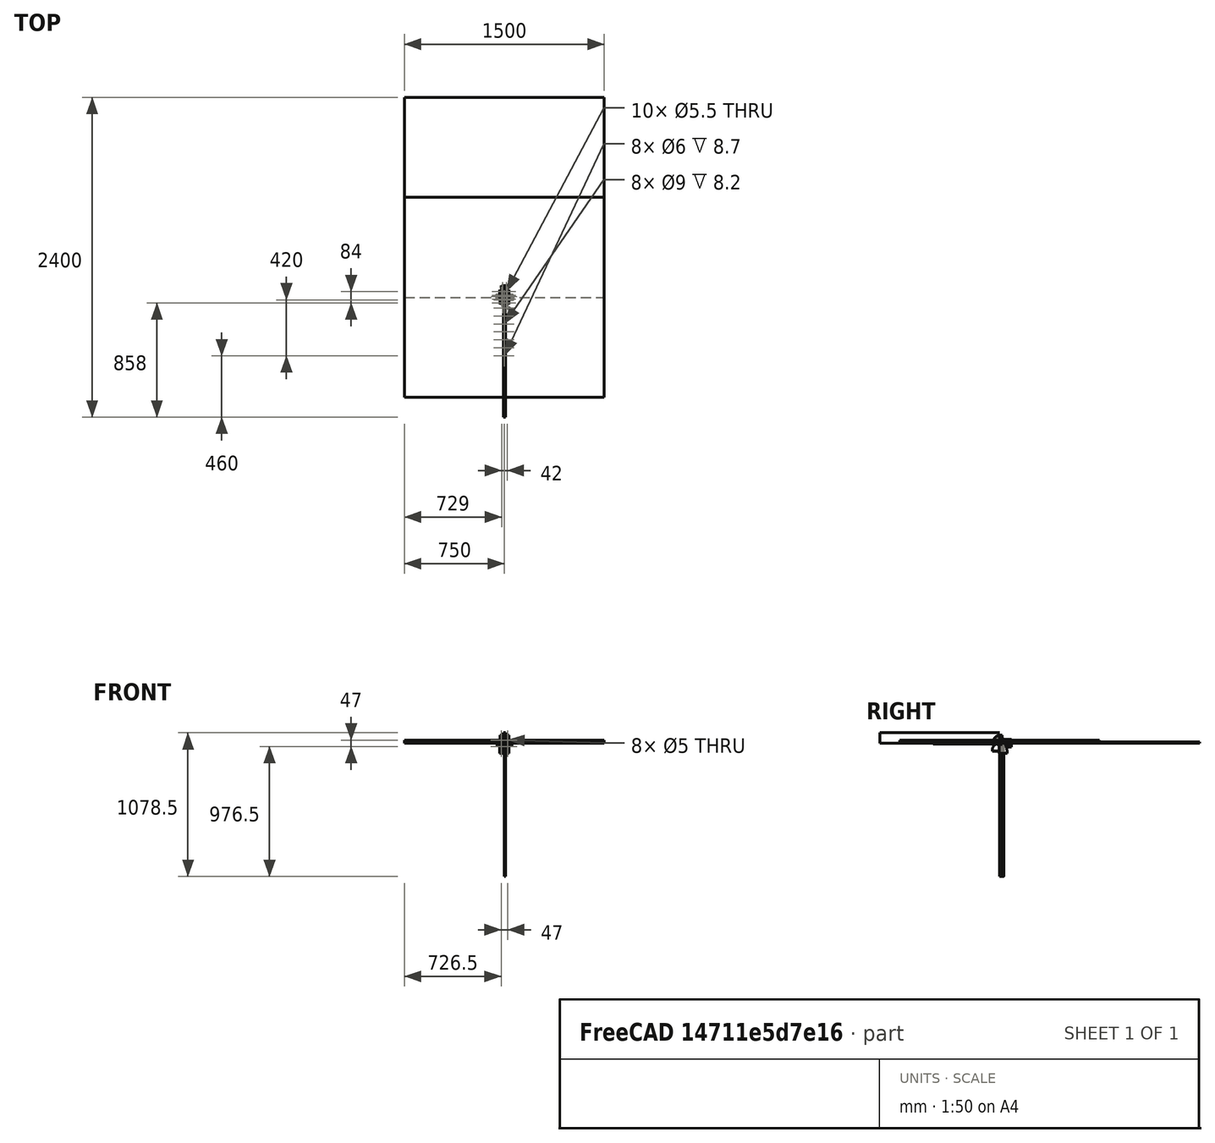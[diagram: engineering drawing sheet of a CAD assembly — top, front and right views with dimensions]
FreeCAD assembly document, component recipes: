
FREECAD ASSEMBLY — COMPONENT RECIPES ("cutting2")

This assembly document has 10 components, labeled P0..P9 below (a component is one placed body or linked part). 7 of them carry a construction recipe — the FreeCAD feature program that regenerates the part from scratch, quoted from this document or its linked companion documents; the rest are supplied as boundary geometry only. No exploded tour is included for this assembly.
COMPONENT P0 — recipe-attached ("p08_bearing_to_plywood", modeled in this document).
Construction recipe (the document's own serialized feature program — sketch geometry with constraints, then the solid features built on it; lengths are millimeters unless a unit is written):

FEATURE [Sketcher::SketchObject] Sketch013
  FullyConstrained = true
  MapMode = 5
  Support = -> [XY_Plane015]
  sketch-geometry (7):
    g0: LineSegment StartX=0 StartY=0 StartZ=0 EndX=27.35 EndY=0 EndZ=0
    g1: LineSegment StartX=27.35 StartY=0 StartZ=0 EndX=27.35 EndY=12.7 EndZ=0
    g2: LineSegment StartX=27.35 StartY=12.7 StartZ=0 EndX=0 EndY=12.7 EndZ=0
    g3: LineSegment StartX=0 StartY=12.7 StartZ=0 EndX=0 EndY=0 EndZ=0
    g4: Circle CenterX=21 CenterY=6.35 CenterZ=0 NormalX=0 NormalY=0 NormalZ=1 AngleXU=0 Radius=2.75
    g5: LineSegment StartX=21 StartY=0 StartZ=0 EndX=21 EndY=6.35 EndZ=0
    g6: LineSegment StartX=21 StartY=6.35 StartZ=0 EndX=21 EndY=12.7 EndZ=0
  constraints (20):
    c: Coincident(g0,g1)
    c: Coincident(g1,g2)
    c: Coincident(g2,g3)
    c: Coincident(g3,g0)
    c: Horizontal(g0)
    c: Horizontal(g2)
    c: Vertical(g1)
    c: Vertical(g3)
    c: Coincident(g0,g-1)
    c: DistanceX(g4) = 21
    c: PointOnObject(g5,g0)
    c: Coincident(g5,g4)
    c: Coincident(g5,g6)
    c: PointOnObject(g6,g2)
    c: Vertical(g6)
    c: Vertical(g5)
    c: Equal(g5,g6)
    c: Diameter(g4) = 5.5
    c: Distance(g3) = 12.7  'length'
    c: DistanceX(g0) = 27.35  'width'
FEATURE [PartDesign::Pad] Pad012
  Direction = (0,0,1)
  Length = 5
  Length2 = 10
  Profile = -> Sketch013
  ReferenceAxis = -> Sketch013 [N_Axis]
  Reversed = true
  Type = 0
FEATURE [Sketcher::SketchObject] Sketch014
  AttachmentOffset = pos=(0,-56,-59.5) rot=(0,0,1;0rad)
  FullyConstrained = true
  MapMode = 5
  Placement = pos=(0,-56,-59.5) rot=(0,0,1;0rad)
  Support = -> [XY_Plane015]
  expr: .AttachmentOffset.Base.y = -.Constraints.length
  expr: .Constraints.length = Sketch010.Constraints[31]
  expr: .Constraints.width = Sketch010.Constraints[30]
  expr: Constraints[33] = Sketch010.Constraints[33]
  sketch-geometry (12):
    g0: LineSegment StartX=0 StartY=0 StartZ=0 EndX=29 EndY=0 EndZ=0
    g1: LineSegment StartX=29 StartY=0 StartZ=0 EndX=29 EndY=56 EndZ=0
    g2: LineSegment StartX=29 StartY=56 StartZ=0 EndX=0 EndY=56 EndZ=0
    g3: LineSegment StartX=0 StartY=56 StartZ=0 EndX=0 EndY=0 EndZ=0
    g4: Circle CenterX=14.5 CenterY=14 CenterZ=0 NormalX=0 NormalY=0 NormalZ=1 AngleXU=0 Radius=2.75
    g5: Circle CenterX=14.5 CenterY=42 CenterZ=0 NormalX=0 NormalY=0 NormalZ=1 AngleXU=0 Radius=2.75
    g6: LineSegment StartX=14.5 StartY=56 StartZ=0 EndX=14.5 EndY=42 EndZ=0
    g7: LineSegment StartX=14.5 StartY=42 StartZ=0 EndX=14.5 EndY=28 EndZ=0
    g8: LineSegment StartX=14.5 StartY=28 StartZ=0 EndX=14.5 EndY=14 EndZ=0
    g9: LineSegment StartX=14.5 StartY=14 StartZ=0 EndX=14.5 EndY=0 EndZ=0
    g10: LineSegment StartX=0 StartY=28 StartZ=0 EndX=14.5 EndY=28 EndZ=0
    g11: LineSegment StartX=14.5 StartY=28 StartZ=0 EndX=29 EndY=28 EndZ=0
  constraints (34):
    c: Coincident(g0,g1)
    c: Coincident(g1,g2)
    c: Coincident(g2,g3)
    c: Coincident(g3,g0)
    c: Horizontal(g0)
    c: Horizontal(g2)
    c: Vertical(g1)
    c: Vertical(g3)
    c: Coincident(g0,g-1)
    c: Vertical(g5,g4)
    c: PointOnObject(g6,g2)
    c: Coincident(g6,g5)
    c: Vertical(g6)
    c: Coincident(g6,g7)
    c: Vertical(g7)
    c: Coincident(g7,g8)
    c: Coincident(g8,g4)
    c: Coincident(g8,g9)
    c: PointOnObject(g9,g0)
    c: Vertical(g9)
    c: Equal(g9,g8)
    c: Equal(g8,g7)
    c: Equal(g7,g6)
    c: PointOnObject(g10,g3)
    c: Coincident(g10,g7)
    c: Horizontal(g10)
    c: Coincident(g10,g11)
    c: PointOnObject(g11,g1)
    c: Horizontal(g11)
    c: Equal(g11,g10)
    c: DistanceX(g0,g0) = 29  'width'
    c: DistanceY(g3,g3) = 56  'length'
    c: Equal(g4,g5)
    c: Diameter(g4) = 5.5
FEATURE [Sketcher::SketchObject] Sketch015
  FullyConstrained = true
  MapMode = 5
  Placement = pos=(0,0,0) rot=(1,0,0;1.5708rad)
  Support = -> [XZ_Plane015]
  expr: Constraints[17] = Sketch013.Constraints[17]
  expr: Constraints[18] = Sketch013.Constraints.length
  expr: Constraints[19] = Sketch013.Constraints.width
  expr: Constraints[23] = Sketch014.AttachmentOffset.Base.z
  expr: Constraints[24] = Sketch014.Constraints.width
  expr: Constraints[9] = Sketch013.Constraints[9]
  sketch-geometry (14):
    g0: LineSegment StartX=0 StartY=0 StartZ=0 EndX=27.35 EndY=0 EndZ=0
    g1: LineSegment StartX=27.35 StartY=0 StartZ=0 EndX=27.35 EndY=12.7 EndZ=0
    g2: LineSegment StartX=27.35 StartY=12.7 StartZ=0 EndX=0 EndY=12.7 EndZ=0
    g3: LineSegment StartX=0 StartY=12.7 StartZ=0 EndX=0 EndY=0 EndZ=0
    g4: Circle CenterX=21 CenterY=6.35 CenterZ=0 NormalX=0 NormalY=0 NormalZ=1 AngleXU=0 Radius=2.75
    g5: LineSegment StartX=21 StartY=0 StartZ=0 EndX=21 EndY=6.35 EndZ=0
    g6: LineSegment StartX=21 StartY=6.35 StartZ=0 EndX=21 EndY=12.7 EndZ=0
    g7: LineSegment StartX=27.35 StartY=0 StartZ=0 EndX=27.35 EndY=-40.764 EndZ=0
    g8: LineSegment StartX=29 StartY=-59.5 StartZ=0 EndX=29 EndY=-54.5 EndZ=0
    g9: ArcOfCircle CenterX=0 CenterY=-54.5 CenterZ=0 NormalX=0 NormalY=0 NormalZ=1 AngleXU=0 Radius=29 StartAngle=0 EndAngle=0.239099
    g10: ArcOfCircle CenterX=56.35 CenterY=-40.764 CenterZ=0 NormalX=0 NormalY=0 NormalZ=1 AngleXU=0 Radius=29 StartAngle=3.14159 EndAngle=3.38069
    g11: LineSegment StartX=27.35 StartY=0 StartZ=0 EndX=0 EndY=0 EndZ=0
    g12: LineSegment StartX=0 StartY=0 StartZ=0 EndX=0 EndY=-59.5 EndZ=0
    g13: LineSegment StartX=0 StartY=-59.5 StartZ=0 EndX=29 EndY=-59.5 EndZ=0
  constraints (39):
    c: Coincident(g0,g1)
    c: Coincident(g1,g2)
    c: Coincident(g2,g3)
    c: Coincident(g3,g0)
    c: Horizontal(g0)
    c: Horizontal(g2)
    c: Vertical(g1)
    c: Vertical(g3)
    c: Coincident(g0,g-1)
    c: DistanceX(g4) = 21
    c: PointOnObject(g5,g0)
    c: Coincident(g5,g4)
    c: Coincident(g5,g6)
    c: PointOnObject(g6,g2)
    c: Vertical(g6)
    c: Vertical(g5)
    c: Equal(g5,g6)
    c: Diameter(g4) = 5.5
    c: Distance(g3) = 12.7
    c: DistanceX(g0) = 27.35
    c: Coincident(g7,g0)
    c: Vertical(g7)
    c: Vertical(g8)
    c: DistanceY(g8) = -59.5
    c: DistanceX(g8) = 29
    c: Distance(g8) = 5
    c: Tangent(g9,g8) = -1.5708
    c: Tangent(g10,g9) = 1.5708
    c: Tangent(g10,g7) = -1.5708
    c: Equal(g9,g10)
    c: PointOnObject(g9,g-2)
    c: Coincident(g7,g11)
    c: PointOnObject(g12,g-2)
    c: PointOnObject(g12,g-2)
    c: Coincident(g12,g13)
    c: Coincident(g13,g8)
    c: Horizontal(g13)
    c: Coincident(g12,g11)
    c: Horizontal(g11)
FEATURE [PartDesign::Pad] Pad013
  BaseFeature = -> Pad012
  Direction = (0,-1,2e-16)
  Length = 5
  Length2 = 10
  Profile = -> Sketch015
  ReferenceAxis = -> Sketch015 [N_Axis]
  Type = 0
FEATURE [PartDesign::Pad] Pad014
  BaseFeature = -> Pad013
  Direction = (0,0,1)
  Length = 5
  Length2 = 10
  Profile = -> Sketch014
  ReferenceAxis = -> Sketch014 [N_Axis]
  Type = 0
FEATURE [Sketcher::SketchObject] Sketch016
  AttachmentOffset = pos=(0,0,24.35) rot=(0,0,1;0rad)
  FullyConstrained = true
  MapMode = 5
  Placement = pos=(24.35,-5.4e-15,5.4e-15) rot=(0.57735,0.57735,0.57735;2.0944rad)
  Support = -> [YZ_Plane015]
  expr: .AttachmentOffset.Base.z = Sketch013.Constraints.width - 3mm
  expr: Constraints[14] = Sketch014.AttachmentOffset.Base.z
  expr: Constraints[15] = Sketch014.Constraints.length
  expr: Constraints[16] = Sketch013.Constraints.length
  sketch-geometry (12):
    g0: LineSegment StartX=-56 StartY=-54.5 StartZ=0 EndX=-56 EndY=-59.5 EndZ=0
    g1: LineSegment StartX=-56 StartY=-59.5 StartZ=0 EndX=0 EndY=-59.5 EndZ=0
    g2: LineSegment StartX=0 StartY=-59.5 StartZ=0 EndX=-2.3e-15 EndY=-17.7 EndZ=0
    g3: LineSegment StartX=12.7 StartY=-5 StartZ=0 EndX=12.7 EndY=0 EndZ=0
    g4: LineSegment StartX=12.7 StartY=0 StartZ=0 EndX=0 EndY=0 EndZ=0
    g5: ArcOfCircle CenterX=0 CenterY=-5 CenterZ=0 NormalX=0 NormalY=0 NormalZ=1 AngleXU=0 Radius=12.7 StartAngle=4.71239 EndAngle=6.28319
    g6: LineSegment StartX=0 StartY=0 StartZ=0 EndX=-5 EndY=0 EndZ=0
    g7: ArcOfEllipse CenterX=-5 CenterY=-54.5 CenterZ=0 NormalX=0 NormalY=0 NormalZ=1 MajorRadius=54.5 MinorRadius=51 AngleXU=1.5708 StartAngle=0 EndAngle=1.5708
    g8: LineSegment StartX=-5 StartY=0 StartZ=0 EndX=-5 EndY=-109 EndZ=0
    g9: LineSegment StartX=-56 StartY=-54.5 StartZ=0 EndX=46 EndY=-54.5 EndZ=0
    g10: GeomPoint X=-5 Y=-35.2841 Z=0
    g11: GeomPoint X=-5 Y=-73.7159 Z=0
  constraints (27):
    c: Vertical(g0)
    c: Coincident(g0,g1)
    c: PointOnObject(g1,g-2)
    c: Horizontal(g1)
    c: Coincident(g1,g2)
    c: PointOnObject(g2,g-2)
    c: PointOnObject(g3,g-1)
    c: Vertical(g3)
    c: Coincident(g3,g4)
    c: Coincident(g4,g-1)
    c: PointOnObject(g5,g-2)
    c: Coincident(g5,g2)
    c: DistanceY(g3,g3) = 5
    c: DistanceY(g0,g0) = 5
    c: DistanceY(g1) = -59.5
    c: Distance(g1) = 56
    c: Distance(g4) = 12.7
    c: Tangent(g5,g3) = -1.5708
    c: Coincident(g6,g4)
    c: PointOnObject(g6,g-1)
    c: Equal(g3,g6)
    c: InternalAlignment(g8-g11 -> g7) x4
    c: Coincident(g7,g9)
    c: Coincident(g7,g0)
    c: Horizontal(g9)
    c: Coincident(g7,g6)
    c: Vertical(g8,g6)
FEATURE [PartDesign::Pad] Pad015
  BaseFeature = -> Pad014
  Direction = (1,-2e-16,3e-16)
  Length = 5
  Length2 = 10
  Profile = -> Sketch016
  ReferenceAxis = -> Sketch016 [N_Axis]
  Type = 0
FEATURE [PartDesign::Mirrored] Mirrored013
  BaseFeature = -> Pad015
  MirrorPlane = -> Sketch013 [V_Axis]
  Originals = -> [Pad012,Pad013,Pad014,Pad015]
FEATURE [PartDesign::Body] Body005  label="p08_bearing_to_plywood"
  Group = -> [Sketch013,Pad012,Sketch014,Sketch015,Pad013,Pad014,Sketch016,Pad015,Mirrored013]
  Origin = -> Origin015
  Tip = -> Mirrored013
COMPONENT P1 — recipe-attached ("bearingTo57BLY", modeled in this document).
Construction recipe (the document's own serialized feature program — sketch geometry with constraints, then the solid features built on it; lengths are millimeters unless a unit is written):

FEATURE [Sketcher::SketchObject] Sketch006
  AttachmentOffset = pos=(0,30,0) rot=(0,0,1;0rad)
  FullyConstrained = true
  MapMode = 5
  Placement = pos=(0,-6.7e-15,30) rot=(1,0,0;1.5708rad)
  Support = -> [XZ_Plane009]
  expr: .AttachmentOffset.Base.y = .Constraints.height
  sketch-geometry (8):
    g0: ArcOfCircle CenterX=0 CenterY=0 CenterZ=0 NormalX=0 NormalY=0 NormalZ=1 AngleXU=0 Radius=19.5 StartAngle=0 EndAngle=1.5708
    g1: LineSegment StartX=28.75 StartY=30 StartZ=0 EndX=28.75 EndY=0 EndZ=0
    g2: LineSegment StartX=19.5 StartY=0 StartZ=0 EndX=28.75 EndY=0 EndZ=0
    g3: LineSegment StartX=23.5 StartY=23.5 StartZ=0 EndX=0 EndY=23.5 EndZ=0
    g4: LineSegment StartX=23.5 StartY=23.5 StartZ=0 EndX=23.5 EndY=0 EndZ=0
    g5: Circle CenterX=23.5 CenterY=23.5 CenterZ=0 NormalX=0 NormalY=0 NormalZ=1 AngleXU=0 Radius=2.75
    g6: LineSegment StartX=28.75 StartY=30 StartZ=0 EndX=0 EndY=30 EndZ=0
    g7: LineSegment StartX=1.2e-15 StartY=19.5 StartZ=0 EndX=0 EndY=30 EndZ=0
  constraints (24):
    c: Coincident(g0,g-1)
    c: PointOnObject(g0,g-1)
    c: PointOnObject(g1,g-1)
    c: Vertical(g1)
    c: Coincident(g2,g0)
    c: Coincident(g2,g1)
    c: PointOnObject(g3,g-2)
    c: Horizontal(g3)
    c: PointOnObject(g4,g-1)
    c: Vertical(g4)
    c: Equal(g4,g3)
    c: DistanceX(g3,g3) = 23.5
    c: Diameter(g0) = 39
    c: DistanceY(g1) = 30  'height'
    c: Coincident(g5,g3)
    c: Coincident(g5,g4)
    c: PointOnObject(g0,g-2)
    c: Coincident(g6,g1)
    c: PointOnObject(g6,g-2)
    c: Horizontal(g6)
    c: Coincident(g7,g0)
    c: Coincident(g7,g6)
    c: Distance(g6) = 28.75  'width'
    c: Diameter(g5) = 5.5
FEATURE [PartDesign::Pad] Pad003
  Direction = (0,-1,-2e-16)
  Length = 5
  Length2 = 10
  Placement = pos=(0,0,0) rot=(1,0,0;1.5708rad)
  Profile = -> Sketch006
  ReferenceAxis = -> Sketch006 [N_Axis]
  Type = 0
FEATURE [PartDesign::Plane] DatumPlane
  AttachmentOffset = pos=(0,0,0) rot=(1,0,0;0.785398rad)
  Length = 86.9918
  MapMode = 5
  Placement = pos=(0,0,0) rot=(1,0,0;0.785398rad)
  ResizeMode = 0
  Support = -> [XY_Plane009]
  Width = 160.206
FEATURE [PartDesign::Mirrored] Mirrored003
  MirrorPlane = -> Sketch006 [V_Axis]
  Placement = pos=(0,0,0) rot=(1,0,0;1.5708rad)
FEATURE [PartDesign::Mirrored] Mirrored004
  MirrorPlane = -> Sketch006 [H_Axis]
  Placement = pos=(0,0,0) rot=(1,0,0;1.5708rad)
FEATURE [PartDesign::MultiTransform] MultiTransform
  BaseFeature = -> Pad003
  Originals = -> [Pad003]
  Placement = pos=(0,0,0) rot=(1,0,0;1.5708rad)
  Transformations = -> [Mirrored003,Mirrored004]
FEATURE [Sketcher::SketchObject] Sketch007
  AttachmentOffset = pos=(0,-29,0) rot=(0,0,1;0rad)
  FullyConstrained = true
  MapMode = 5
  Placement = pos=(0,-29,0) rot=(0,0,1;0rad)
  Support = -> [XY_Plane009]
  expr: .AttachmentOffset.Base.y = -.Constraints.length - 5mm
  expr: .Constraints.width = Sketch006.Constraints.width
  sketch-geometry (7):
    g0: Circle CenterX=18 CenterY=16 CenterZ=0 NormalX=0 NormalY=0 NormalZ=1 AngleXU=0 Radius=2.5
    g1: LineSegment StartX=0 StartY=0 StartZ=0 EndX=28.75 EndY=0 EndZ=0
    g2: LineSegment StartX=28.75 StartY=0 StartZ=0 EndX=28.75 EndY=24 EndZ=0
    g3: LineSegment StartX=28.75 StartY=24 StartZ=0 EndX=0 EndY=24 EndZ=0
    g4: LineSegment StartX=0 StartY=24 StartZ=0 EndX=0 EndY=0 EndZ=0
    g5: LineSegment StartX=18 StartY=16 StartZ=0 EndX=18 EndY=24 EndZ=0
    g6: LineSegment StartX=18 StartY=16 StartZ=0 EndX=28.75 EndY=16 EndZ=0
  constraints (20):
    c: DistanceX(g0) = 18
    c: DistanceY(g0) = 16
    c: Diameter(g0) = 5
    c: Coincident(g1,g2)
    c: Coincident(g2,g3)
    c: Coincident(g3,g4)
    c: Coincident(g4,g1)
    c: Horizontal(g1)
    c: Horizontal(g3)
    c: Vertical(g2)
    c: Vertical(g4)
    c: Coincident(g1,g-1)
    c: Coincident(g5,g0)
    c: PointOnObject(g5,g3)
    c: Vertical(g5)
    c: Coincident(g6,g0)
    c: PointOnObject(g6,g2)
    c: Horizontal(g6)
    c: Distance(g2) = 24  'length'
    c: DistanceX(g2) = 28.75  'width'
FEATURE [PartDesign::AdditiveBox] Box
  AttacherType = Attacher::AttachEngine3D
  AttachmentOffset = pos=(0,-5,-5) rot=(0,0,1;0rad)
  BaseFeature = -> MultiTransform
  Height = 5
  Length = 32.75
  MapMode = 5
  Placement = pos=(0,-5,-5) rot=(0,0,1;0rad)
  Support = -> [XY_Plane008]
  Width = 5
FEATURE [PartDesign::Mirrored] Mirrored005
  BaseFeature = -> Box
  MirrorPlane = -> YZ_Plane009
  Originals = -> [Box]
  Placement = pos=(0,-5,-5) rot=(0,0,1;0rad)
FEATURE [PartDesign::Pad] Pad004
  BaseFeature = -> Mirrored005
  Direction = (0,0,1)
  Length = 5
  Length2 = 10
  Placement = pos=(0,-5,-5) rot=(0,0,1;0rad)
  Profile = -> Sketch007
  ReferenceAxis = -> Sketch007 [N_Axis]
  Reversed = true
  Type = 0
FEATURE [PartDesign::Mirrored] Mirrored006
  MirrorPlane = -> Sketch007 [V_Axis]
  Placement = pos=(0,-5,-5) rot=(0,0,1;0rad)
FEATURE [PartDesign::Mirrored] Mirrored007
  MirrorPlane = -> Sketch007 [H_Axis]
  Placement = pos=(0,-5,-5) rot=(0,0,1;0rad)
FEATURE [PartDesign::MultiTransform] MultiTransform001
  BaseFeature = -> Pad004
  Originals = -> [Pad004]
  Placement = pos=(0,-5,-5) rot=(0,0,1;0rad)
  Transformations = -> [Mirrored006,Mirrored007]
FEATURE [Sketcher::SketchObject] Sketch008
  AttachmentOffset = pos=(0,0,28.75) rot=(0,0,1;0rad)
  FullyConstrained = false
  MapMode = 5
  Placement = pos=(28.75,-6.4e-15,6.4e-15) rot=(0.57735,0.57735,0.57735;2.0944rad)
  Support = -> [YZ_Plane009]
  expr: .AttachmentOffset.Base.z = Sketch006.Constraints.width
  expr: Constraints[12] = -(Sketch007.Constraints.length * 2 + 5mm)
  expr: Constraints[8] = Sketch006.Constraints.height * 2
  sketch-geometry (9):
    g0: LineSegment StartX=0 StartY=60 StartZ=0 EndX=-5 EndY=60 EndZ=0
    g1: LineSegment StartX=-53 StartY=1.12207e-11 StartZ=0 EndX=-53 EndY=-5 EndZ=0
    g2: LineSegment StartX=-53 StartY=-5 StartZ=0 EndX=0 EndY=-5 EndZ=0
    g3: LineSegment StartX=0 StartY=-5 StartZ=0 EndX=0 EndY=60 EndZ=0
    g4: ArcOfEllipse CenterX=9.28498 CenterY=2.81547e-11 CenterZ=0 NormalX=0 NormalY=0 NormalZ=1 MajorRadius=62.285 MinorRadius=61.6431 AngleXU=9.37e-14 StartAngle=1.8022 EndAngle=3.14159
    g5: LineSegment StartX=71.57 StartY=3.43634e-11 StartZ=0 EndX=-53 EndY=1.12207e-11 EndZ=0
    g6: LineSegment StartX=9.28498 StartY=61.6431 StartZ=0 EndX=9.28498 EndY=-61.6431 EndZ=0
    g7: GeomPoint X=18.2036 Y=2.89902e-11 Z=0
    g8: GeomPoint X=0.366367 Y=2.76194e-11 Z=0
  constraints (18):
    c: PointOnObject(g0,g-2)
    c: PointOnObject(g1,g-1)
    c: Coincident(g1,g2)
    c: PointOnObject(g2,g-2)
    c: Horizontal(g2)
    c: Coincident(g2,g3)
    c: Coincident(g3,g0)
    c: DistanceY(g2) = -5
    c: DistanceY(g0) = 60
    c: Vertical(g1)
    c: DistanceX(g0) = -5
    c: Horizontal(g0)
    c: DistanceX(g1) = -53
    c: InternalAlignment(g5-g8 -> g4) x4
    c: Vertical(g6)
    c: Coincident(g4,g1)
    c: Coincident(g4,g0)
    c: Coincident(g5,g1)
FEATURE [PartDesign::Pad] Pad005
  BaseFeature = -> MultiTransform001
  Direction = (1,-2e-16,3e-16)
  Length = 5
  Length2 = 10
  Placement = pos=(0,-5,-5) rot=(0,0,1;0rad)
  Profile = -> Sketch008
  ReferenceAxis = -> Sketch008 [N_Axis]
  Type = 0
FEATURE [PartDesign::Mirrored] Mirrored008
  BaseFeature = -> Pad005
  MirrorPlane = -> YZ_Plane009
  Originals = -> [Pad005]
  Placement = pos=(0,-5,-5) rot=(0,0,1;0rad)
FEATURE [Sketcher::SketchObject] Sketch009
  FullyConstrained = true
  MapMode = 5
  Support = -> [XY_Plane009]
  expr: Constraints[16] = -Sketch007.Constraints.length * 2 - 5mm
  expr: Constraints[17] = Sketch007.Constraints.width
  sketch-geometry (10):
    g0: LineSegment StartX=0 StartY=-72 StartZ=0 EndX=28.75 EndY=-72 EndZ=0
    g1: LineSegment StartX=28.75 StartY=-72 StartZ=0 EndX=28.75 EndY=-53 EndZ=0
    g2: LineSegment StartX=28.75 StartY=-53 StartZ=0 EndX=0 EndY=-53 EndZ=0
    g3: LineSegment StartX=0 StartY=-53 StartZ=0 EndX=0 EndY=-72 EndZ=0
    g4: LineSegment StartX=28.75 StartY=-89 StartZ=0 EndX=0 EndY=-89 EndZ=0
    g5: LineSegment StartX=0 StartY=-89 StartZ=0 EndX=0 EndY=-72 EndZ=0
    g6: Circle CenterX=24.75 CenterY=-80.5 CenterZ=0 NormalX=0 NormalY=0 NormalZ=1 AngleXU=0 Radius=1.375
    g7: Circle CenterX=16.75 CenterY=-80.5 CenterZ=0 NormalX=0 NormalY=0 NormalZ=1 AngleXU=0 Radius=1.375
    g8: LineSegment StartX=28.75 StartY=-72 StartZ=0 EndX=28.75 EndY=-80.5 EndZ=0
    g9: LineSegment StartX=28.75 StartY=-80.5 StartZ=0 EndX=28.75 EndY=-89 EndZ=0
  constraints (29):
    c: Coincident(g0,g1)
    c: Coincident(g1,g2)
    c: Coincident(g2,g3)
    c: Coincident(g3,g0)
    c: Horizontal(g0)
    c: Horizontal(g2)
    c: Vertical(g1)
    c: Vertical(g3)
    c: PointOnObject(g0,g-2)
    c: DistanceY(g0) = -72
    c: Coincident(g1,g8)
    c: Coincident(g9,g4)
    c: PointOnObject(g4,g-2)
    c: Horizontal(g4)
    c: Coincident(g4,g5)
    c: Coincident(g5,g3)
    c: DistanceY(g2) = -53
    c: Distance(g2) = 28.75
    c: Distance(g5) = 17
    c: Coincident(g8,g9)
    c: Vertical(g8)
    c: Vertical(g9)
    c: Equal(g9,g8)
    c: Horizontal(g8,g6)
    c: Horizontal(g6,g7)
    c: Equal(g6,g7)
    c: Diameter(g6) = 2.75
    c: Distance(g6,g8) = 4
    c: Distance(g6,g7) = 8
FEATURE [PartDesign::Pad] Pad006
  BaseFeature = -> Mirrored008
  Direction = (0,0,1)
  Length = 5
  Length2 = 10
  Placement = pos=(0,-5,-5) rot=(0,0,1;0rad)
  Profile = -> Sketch009
  ReferenceAxis = -> Sketch009 [N_Axis]
  Reversed = true
  Type = 0
FEATURE [PartDesign::Body] Body004
  Group = -> [Sketch006,Pad003,DatumPlane,MultiTransform,Mirrored003,Mirrored004,Sketch007,Box,Mirrored005,Pad004,MultiTransform001,Mirrored006,Mirrored007,Sketch008,Pad005,Mirrored008,Sketch009,Pad006]
  Origin = -> Origin009
  Tip = -> Pad006
COMPONENT P2 — geometry summary ("rail"; no construction recipe available for this part):
  bounding box: 500.0 x 20.0 x 17.5 mm
  tessellated surface: 1,522 triangles
  volume: 144383 mm^3 (83% of its bounding box)
  symmetry: 2-fold rotationally symmetric about the y axis; mirror-symmetric across its x mid-plane, z mid-plane
COMPONENT P3 — recipe-attached ("57ToPlywood", modeled in this document).
Construction recipe (the document's own serialized feature program — sketch geometry with constraints, then the solid features built on it; lengths are millimeters unless a unit is written):

FEATURE [PartDesign::CoordinateSystem] LCS_0004
  AttacherType = Attacher::AttachEngine3D
  MapMode = 2
  Support = -> [X_Axis012]
FEATURE [Sketcher::SketchObject] Sketch010
  AttachmentOffset = pos=(0,0,-74.5) rot=(0,0,1;0rad)
  FullyConstrained = true
  MapMode = 5
  Placement = pos=(0,0,-74.5) rot=(0,0,1;0rad)
  Support = -> [XY_Plane012]
  expr: .AttachmentOffset.Base.z = -74.5
  expr: Constraints[30] = Sketch011.Constraints.width
  sketch-geometry (12):
    g0: LineSegment StartX=0 StartY=0 StartZ=0 EndX=29 EndY=0 EndZ=0
    g1: LineSegment StartX=29 StartY=0 StartZ=0 EndX=29 EndY=56 EndZ=0
    g2: LineSegment StartX=29 StartY=56 StartZ=0 EndX=0 EndY=56 EndZ=0
    g3: LineSegment StartX=0 StartY=56 StartZ=0 EndX=0 EndY=0 EndZ=0
    g4: Circle CenterX=14.5 CenterY=14 CenterZ=0 NormalX=0 NormalY=0 NormalZ=1 AngleXU=0 Radius=2.75
    g5: Circle CenterX=14.5 CenterY=42 CenterZ=0 NormalX=0 NormalY=0 NormalZ=1 AngleXU=0 Radius=2.75
    g6: LineSegment StartX=14.5 StartY=56 StartZ=0 EndX=14.5 EndY=42 EndZ=0
    g7: LineSegment StartX=14.5 StartY=42 StartZ=0 EndX=14.5 EndY=28 EndZ=0
    g8: LineSegment StartX=14.5 StartY=28 StartZ=0 EndX=14.5 EndY=14 EndZ=0
    g9: LineSegment StartX=14.5 StartY=14 StartZ=0 EndX=14.5 EndY=0 EndZ=0
    g10: LineSegment StartX=0 StartY=28 StartZ=0 EndX=14.5 EndY=28 EndZ=0
    g11: LineSegment StartX=14.5 StartY=28 StartZ=0 EndX=29 EndY=28 EndZ=0
  constraints (34):
    c: Coincident(g0,g1)
    c: Coincident(g1,g2)
    c: Coincident(g2,g3)
    c: Coincident(g3,g0)
    c: Horizontal(g0)
    c: Horizontal(g2)
    c: Vertical(g1)
    c: Vertical(g3)
    c: Coincident(g0,g-1)
    c: Vertical(g5,g4)
    c: PointOnObject(g6,g2)
    c: Coincident(g6,g5)
    c: Vertical(g6)
    c: Coincident(g6,g7)
    c: Vertical(g7)
    c: Coincident(g7,g8)
    c: Coincident(g8,g4)
    c: Coincident(g8,g9)
    c: PointOnObject(g9,g0)
    c: Vertical(g9)
    c: Equal(g9,g8)
    c: Equal(g8,g7)
    c: Equal(g7,g6)
    c: PointOnObject(g10,g3)
    c: Coincident(g10,g7)
    c: Horizontal(g10)
    c: Coincident(g10,g11)
    c: PointOnObject(g11,g1)
    c: Horizontal(g11)
    c: Equal(g11,g10)
    c: DistanceX(g0,g0) = 29
    c: DistanceY(g3,g3) = 56
    c: Equal(g4,g5)
    c: Diameter(g4) = 5.5
FEATURE [Sketcher::SketchObject] Sketch011
  FullyConstrained = true
  MapMode = 5
  Placement = pos=(0,0,0) rot=(1,0,0;1.5708rad)
  Support = -> [XZ_Plane012]
  sketch-geometry (8):
    g0: Circle CenterX=23.5 CenterY=23.5 CenterZ=0 NormalX=0 NormalY=0 NormalZ=1 AngleXU=0 Radius=2.5
    g1: LineSegment StartX=29 StartY=29 StartZ=0 EndX=0 EndY=29 EndZ=0
    g2: LineSegment StartX=29 StartY=29 StartZ=0 EndX=29 EndY=0 EndZ=0
    g3: ArcOfCircle CenterX=0 CenterY=0 CenterZ=0 NormalX=0 NormalY=0 NormalZ=1 AngleXU=0 Radius=20 StartAngle=0 EndAngle=1.5708
    g4: LineSegment StartX=20 StartY=0 StartZ=0 EndX=29 EndY=0 EndZ=0
    g5: LineSegment StartX=1.2e-15 StartY=20 StartZ=0 EndX=0 EndY=29 EndZ=0
    g6: LineSegment StartX=0 StartY=0 StartZ=0 EndX=29 EndY=0 EndZ=0
    g7: LineSegment StartX=0 StartY=0 StartZ=0 EndX=0 EndY=29 EndZ=0
  constraints (22):
    c: PointOnObject(g1,g-2)
    c: Horizontal(g1)
    c: Coincident(g3,g-1)
    c: PointOnObject(g3,g-2)
    c: PointOnObject(g3,g-1)
    c: Diameter(g3) = 40
    c: Coincident(g4,g3)
    c: Coincident(g4,g2)
    c: Horizontal(g4)
    c: Coincident(g5,g3)
    c: Coincident(g5,g1)
    c: DistanceX(g0) = 23.5
    c: DistanceY(g0) = 23.5
    c: Diameter(g0) = 5
    c: Vertical(g2)
    c: Coincident(g6,g3)
    c: Coincident(g6,g2)
    c: Coincident(g7,g3)
    c: Coincident(g7,g1)
    c: Equal(g6,g7)
    c: Distance(g6) = 29  'width'
    c: Coincident(g2,g1)
FEATURE [PartDesign::Pad] Pad007
  Direction = (0,-1,-2e-16)
  Length = 5
  Length2 = 10
  Placement = pos=(0,0,0) rot=(1,0,0;1.5708rad)
  Profile = -> Sketch011
  ReferenceAxis = -> Sketch011 [N_Axis]
  Type = 0
FEATURE [PartDesign::Mirrored] Mirrored009
  MirrorPlane = -> Sketch011 [V_Axis]
  Placement = pos=(0,0,0) rot=(1,0,0;1.5708rad)
FEATURE [PartDesign::Mirrored] Mirrored010
  MirrorPlane = -> Sketch011 [H_Axis]
  Placement = pos=(0,0,0) rot=(1,0,0;1.5708rad)
FEATURE [PartDesign::MultiTransform] MultiTransform002
  BaseFeature = -> Pad007
  Originals = -> [Pad007]
  Placement = pos=(0,0,0) rot=(1,0,0;1.5708rad)
  Transformations = -> [Mirrored009,Mirrored010]
FEATURE [Sketcher::SketchObject] Sketch_1
  FullyConstrained = true
  MapMode = 5
  Placement = pos=(0,0,0) rot=(1,0,0;1.5708rad)
  Support = -> [XZ_Plane012]
  expr: Constraints[10] = Sketch010.AttachmentOffset.Base.z
  expr: Constraints[11] = -Sketch011.Constraints.width
  expr: Constraints[9] = Sketch011.Constraints.width
  sketch-geometry (4):
    g0: LineSegment StartX=0 StartY=-29 StartZ=0 EndX=29 EndY=-29 EndZ=0
    g1: LineSegment StartX=29 StartY=-29 StartZ=0 EndX=29 EndY=-74.5 EndZ=0
    g2: LineSegment StartX=29 StartY=-74.5 StartZ=0 EndX=0 EndY=-74.5 EndZ=0
    g3: LineSegment StartX=0 StartY=-74.5 StartZ=0 EndX=0 EndY=-29 EndZ=0
  constraints (12):
    c: Coincident(g0,g1)
    c: Coincident(g1,g2)
    c: Coincident(g2,g3)
    c: Coincident(g3,g0)
    c: Horizontal(g0)
    c: Horizontal(g2)
    c: Vertical(g1)
    c: Vertical(g3)
    c: PointOnObject(g0,g-2)
    c: Distance(g0) = 29
    c: DistanceY(g2) = -74.5
    c: DistanceY(g0) = -29
FEATURE [PartDesign::Pad] Pad008
  BaseFeature = -> MultiTransform002
  Direction = (0,-1,-2e-16)
  Length = 5
  Length2 = 10
  Placement = pos=(0,0,0) rot=(1,0,0;1.5708rad)
  Profile = -> Sketch_1
  ReferenceAxis = -> Sketch_1 [N_Axis]
  Type = 0
FEATURE [PartDesign::Pad] Pad009
  BaseFeature = -> Pad008
  Direction = (0,0,1)
  Length = 5
  Length2 = 10
  Placement = pos=(0,0,0) rot=(1,0,0;1.5708rad)
  Profile = -> Sketch010
  ReferenceAxis = -> Sketch010 [N_Axis]
  Type = 0
FEATURE [PartDesign::Mirrored] Mirrored011
  BaseFeature = -> Pad009
  MirrorPlane = -> Sketch_1 [V_Axis]
  Originals = -> [Pad008,Pad009]
  Placement = pos=(0,0,0) rot=(1,0,0;1.5708rad)
FEATURE [Sketcher::SketchObject] Sketch012
  AttachmentOffset = pos=(0,0,29) rot=(0,0,1;0rad)
  FullyConstrained = true
  MapMode = 5
  Placement = pos=(29,-6.4e-15,6.4e-15) rot=(0.57735,0.57735,0.57735;2.0944rad)
  Support = -> [YZ_Plane012]
  expr: .AttachmentOffset.Base.z = Sketch011.Constraints.width
  expr: Constraints[10] = Sketch010.AttachmentOffset.Base.z + 5mm
  expr: Constraints[12] = 56
  expr: Constraints[9] = Sketch011.Constraints.width
  sketch-geometry (9):
    g0: LineSegment StartX=0 StartY=29 StartZ=0 EndX=-5 EndY=29 EndZ=0
    g1: LineSegment StartX=-5 StartY=29 StartZ=0 EndX=-5 EndY=-74.5 EndZ=0
    g2: LineSegment StartX=-5 StartY=-74.5 StartZ=0 EndX=56 EndY=-74.5 EndZ=0
    g3: LineSegment StartX=56 StartY=-74.5 StartZ=0 EndX=56 EndY=-69.5 EndZ=0
    g4: ArcOfEllipse CenterX=0 CenterY=-69.5 CenterZ=0 NormalX=0 NormalY=0 NormalZ=1 MajorRadius=98.5 MinorRadius=56 AngleXU=-1.5708 StartAngle=1.5708 EndAngle=3.14159
    g5: LineSegment StartX=0 StartY=-168 StartZ=0 EndX=0 EndY=29 EndZ=0
    g6: LineSegment StartX=56 StartY=-69.5 StartZ=0 EndX=-56 EndY=-69.5 EndZ=0
    g7: GeomPoint X=0 Y=-150.532 Z=0
    g8: GeomPoint X=0 Y=11.5324 Z=0
  constraints (19):
    c: PointOnObject(g0,g-2)
    c: Coincident(g0,g1)
    c: Vertical(g1)
    c: Coincident(g1,g2)
    c: Horizontal(g2)
    c: Coincident(g2,g3)
    c: Vertical(g3)
    c: Horizontal(g0)
    c: Equal(g3,g0)
    c: DistanceY(g0) = 29
    c: DistanceY(g3) = -69.5
    c: Distance(g3) = 5
    c: DistanceX(g3) = 56
    c: InternalAlignment(g5-g8 -> g4) x4
    c: PointOnObject(g4,g-2)
    c: Coincident(g4,g0)
    c: Coincident(g4,g3)
    c: Vertical(g5)
    c: DistanceY(g1,g4) = 5
FEATURE [PartDesign::Pad] Pad010
  BaseFeature = -> Mirrored011
  Direction = (1,-2e-16,3e-16)
  Length = 5
  Length2 = 10
  Placement = pos=(0,0,0) rot=(1,0,0;1.5708rad)
  Profile = -> Sketch012
  ReferenceAxis = -> Sketch012 [N_Axis]
  Type = 0
FEATURE [PartDesign::Mirrored] Mirrored012
  BaseFeature = -> Pad010
  MirrorPlane = -> YZ_Plane012
  Originals = -> [Pad010]
  Placement = pos=(0,0,0) rot=(1,0,0;1.5708rad)
FEATURE [PartDesign::CoordinateSystem] Local_CS  label="fixture_plane"
  AttacherType = Attacher::AttachEngine3D
  AttachmentOffset = pos=(0,0,0) rot=(-1,0,0;1.5708rad)
  MapMode = 5
  Placement = pos=(0,0,0) rot=(-1,0,0;1.5708rad)
  Support = -> [XY_Plane012]
FEATURE [PartDesign::Body] _7ToPlywood  label="57ToPlywood"
  Group = -> [LCS_0004,Sketch010,Sketch011,Pad007,MultiTransform002,Mirrored009,Mirrored010,Sketch_1,Pad008,Pad009,Mirrored011,Sketch012,Pad010,Mirrored012,Local_CS]
  Origin = -> Origin012
  Tip = -> Mirrored012
COMPONENT P4 — recipe-attached ("bearing", modeled in this document).
Construction recipe (the document's own serialized feature program — sketch geometry with constraints, then the solid features built on it; lengths are millimeters unless a unit is written):

FEATURE [Sketcher::SketchObject] Sketch
  FullyConstrained = false
  MapMode = 5
  Placement = pos=(0,0,0) rot=(1,0,0;1.5708rad)
  Support = -> [XZ_Plane]
  sketch-geometry (12):
    g0: LineSegment StartX=0 StartY=23 StartZ=0 EndX=0 EndY=0 EndZ=0
    g1: ArcOfCircle CenterX=0 CenterY=33 CenterZ=0 NormalX=0 NormalY=0 NormalZ=1 AngleXU=0 Radius=10 StartAngle=4.71239 EndAngle=7.85398
    g2: ArcOfCircle CenterX=0 CenterY=33 CenterZ=0 NormalX=0 NormalY=0 NormalZ=1 AngleXU=0 Radius=29 StartAngle=0.169407 EndAngle=1.5708
    g3: ArcOfCircle CenterX=62.5 CenterY=12.5 CenterZ=0 NormalX=0 NormalY=0 NormalZ=1 AngleXU=0 Radius=2.5 StartAngle=0 EndAngle=1.5708
    g4: LineSegment StartX=0 StartY=0 StartZ=0 EndX=65 EndY=0 EndZ=0
    g5: LineSegment StartX=65 StartY=0 StartZ=0 EndX=65 EndY=12.5 EndZ=0
    g6: LineSegment StartX=3.1e-15 StartY=43 StartZ=0 EndX=0 EndY=62 EndZ=0
    g7: LineSegment StartX=17 StartY=33 StartZ=0 EndX=17 EndY=0 EndZ=0
    g8: LineSegment StartX=32.5 StartY=15 StartZ=0 EndX=47.5 EndY=15 EndZ=0
    g9: LineSegment StartX=47.5 StartY=15 StartZ=0 EndX=62.5 EndY=15 EndZ=0
    g10: LineSegment StartX=47.5 StartY=0 StartZ=0 EndX=47.5 EndY=15 EndZ=0
    g11: LineSegment StartX=32.5 StartY=15 StartZ=0 EndX=28.5849 EndY=37.8893 EndZ=0
  constraints (33):
    c: PointOnObject(g0,g-2)
    c: Coincident(g0,g-1)
    c: PointOnObject(g1,g-2)
    c: Coincident(g1,g0)
    c: PointOnObject(g1,g-2)
    c: Coincident(g2,g1)
    c: PointOnObject(g2,g-2)
    c: Coincident(g4,g0)
    c: PointOnObject(g4,g-1)
    c: Coincident(g5,g4)
    c: Vertical(g5)
    c: Coincident(g6,g1)
    c: Coincident(g6,g2)
    c: Tangent(g5,g3) = -1.5708
    c: Tangent(g9,g3) = 1.5708
    c: PointOnObject(g7,g-1)
    c: Vertical(g7)
    c: Diameter(g1) = 20  'd'
    c: Coincident(g8,g9)
    c: Horizontal(g8)
    c: Horizontal(g9)
    c: Equal(g8,g9)
    c: PointOnObject(g10,g-1)
    c: Coincident(g10,g8)
    c: Vertical(g10)
    c: Distance(g10) = 15  'fixture_hole_height'
    c: DistanceX(g10) = 47.5  'hole_d_x2'
    c: DistanceX(g4) = 65  'width_x2'
    c: DistanceY(g1) = 33
    c: DistanceY(g2) = 62
    c: Coincident(g11,g8)
    c: Tangent(g11,g2) = -1.5708
    c: Diameter(g3) = 5
FEATURE [PartDesign::Pad] Pad  label="bearing_fixture_pad"
  Direction = (0,-1,-2e-16)
  Length = 40
  Length2 = 10
  Midplane = true
  Placement = pos=(0,0,0) rot=(1,0,0;1.5708rad)
  Profile = -> Sketch
  ReferenceAxis = -> Sketch [N_Axis]
  Type = 0
FEATURE [Sketcher::SketchObject] Sketch001
  FullyConstrained = true
  MapMode = 5
  Support = -> [XY_Plane]
  expr: Constraints[14] = Sketch.Constraints.hole_d_x2
  sketch-geometry (7):
    g0: ArcOfCircle CenterX=45 CenterY=0 CenterZ=0 NormalX=0 NormalY=0 NormalZ=1 AngleXU=0 Radius=5 StartAngle=1.5708 EndAngle=4.71239
    g1: ArcOfCircle CenterX=50 CenterY=0 CenterZ=0 NormalX=0 NormalY=0 NormalZ=1 AngleXU=0 Radius=5 StartAngle=4.71239 EndAngle=7.85398
    g2: LineSegment StartX=45 StartY=-5 StartZ=0 EndX=50 EndY=-5 EndZ=0
    g3: LineSegment StartX=50 StartY=5 StartZ=0 EndX=45 EndY=5 EndZ=0
    g4: GeomPoint X=40 Y=0 Z=0
    g5: GeomPoint X=55 Y=0 Z=0
    g6: GeomPoint X=47.5 Y=0 Z=0
  constraints (15):
    c: Tangent(g0,g2) = -1.5708
    c: Tangent(g2,g1) = -1.5708
    c: Tangent(g1,g3) = -1.5708
    c: Tangent(g3,g0) = -1.5708
    c: Equal(g0,g1)
    c: PointOnObject(g0,g-1)
    c: PointOnObject(g1,g-1)
    c: PointOnObject(g4,g0)
    c: PointOnObject(g5,g1)
    c: PointOnObject(g5,g-1)
    c: PointOnObject(g4,g-1)
    c: Diameter(g1) = 10
    c: DistanceX(g4,g5) = 15
    c: Symmetric(g0,g1,g6)
    c: DistanceX(g6) = 47.5
FEATURE [PartDesign::Pocket] Pocket
  BaseFeature = -> Pad
  Direction = (0,0,-1)
  Length = 5
  Length2 = 5
  Placement = pos=(0,0,0) rot=(1,0,0;1.5708rad)
  Profile = -> Sketch001
  ReferenceAxis = -> Sketch001 [N_Axis]
  Reversed = true
  Type = 1
FEATURE [PartDesign::Mirrored] Mirrored
  BaseFeature = -> Pocket
  MirrorPlane = -> Sketch [V_Axis]
  Originals = -> [Pad,Pocket]
  Placement = pos=(0,0,0) rot=(1,0,0;1.5708rad)
FEATURE [PartDesign::Fillet] Fillet
  Base = -> Mirrored [Edge18,Edge9]
  BaseFeature = -> Mirrored
  Placement = pos=(0,0,0) rot=(1,0,0;1.5708rad)
  Radius = 4
  SupportTransform = false
  UseAllEdges = false
FEATURE [PartDesign::Body] Body  label="bearing_fixture_body"
  Group = -> [Sketch,Pad,Sketch001,Pocket,Mirrored,Fillet]
  Origin = -> Origin
  Tip = -> Fillet
FEATURE [Sketcher::SketchObject] Sketch003
  FullyConstrained = true
  MapMode = 5
  Support = -> [XY_Plane001]
  expr: Constraints[11] = Sketch001.Constraints[11]
  expr: Constraints[12] = Sketch001.Constraints[12]
  expr: Constraints[14] = Sketch001.Constraints[14]
  expr: Constraints[26] = Sketch.Constraints.width_x2
  expr: Constraints[27] = Pad.Length
  sketch-geometry (12):
    g0: ArcOfCircle CenterX=45 CenterY=0 CenterZ=0 NormalX=0 NormalY=0 NormalZ=1 AngleXU=0 Radius=5 StartAngle=1.5708 EndAngle=4.71239
    g1: ArcOfCircle CenterX=50 CenterY=0 CenterZ=0 NormalX=0 NormalY=0 NormalZ=1 AngleXU=0 Radius=5 StartAngle=4.71239 EndAngle=7.85398
    g2: LineSegment StartX=45 StartY=-5 StartZ=0 EndX=50 EndY=-5 EndZ=0
    g3: LineSegment StartX=50 StartY=5 StartZ=0 EndX=45 EndY=5 EndZ=0
    g4: GeomPoint X=40 Y=0 Z=0
    g5: GeomPoint X=55 Y=0 Z=0
    g6: GeomPoint X=47.5 Y=0 Z=0
    g7: LineSegment StartX=65 StartY=-20 StartZ=0 EndX=65 EndY=20 EndZ=0
    g8: LineSegment StartX=65 StartY=20 StartZ=0 EndX=0 EndY=20 EndZ=0
    g9: LineSegment StartX=0 StartY=20 StartZ=0 EndX=0 EndY=-20 EndZ=0
    g10: LineSegment StartX=0 StartY=-20 StartZ=0 EndX=65 EndY=-20 EndZ=0
    g11: GeomPoint X=32.5 Y=0 Z=0
  constraints (28):
    c: Tangent(g0,g2) = -1.5708
    c: Tangent(g2,g1) = -1.5708
    c: Tangent(g1,g3) = -1.5708
    c: Tangent(g3,g0) = -1.5708
    c: Equal(g0,g1)
    c: PointOnObject(g0,g-1)
    c: PointOnObject(g1,g-1)
    c: PointOnObject(g4,g0)
    c: PointOnObject(g5,g1)
    c: PointOnObject(g5,g-1)
    c: PointOnObject(g4,g-1)
    c: Diameter(g1) = 10
    c: DistanceX(g4,g5) = 15
    c: Symmetric(g0,g1,g6)
    c: DistanceX(g6) = 47.5
    c: Coincident(g7,g8)
    c: Coincident(g8,g9)
    c: Coincident(g9,g10)
    c: Coincident(g10,g7)
    c: Horizontal(g8)
    c: Horizontal(g10)
    c: Vertical(g7)
    c: Vertical(g9)
    c: Symmetric(g8,g7,g11)
    c: PointOnObject(g11,g-1)
    c: PointOnObject(g8,g-2)
    c: Distance(g-1,g7) = 65
    c: DistanceY(g9,g9) = 40
FEATURE [PartDesign::Pad] Pad001  label="insertion_pad"
  Direction = (0,0,1)
  Length = 8
  Length2 = 10
  Profile = -> Sketch003
  ReferenceAxis = -> Sketch003 [N_Axis]
  Reversed = true
  Type = 0
FEATURE [PartDesign::Mirrored] Mirrored001
  BaseFeature = -> Pad001
  MirrorPlane = -> Sketch003 [V_Axis]
  Originals = -> [Pad001]
FEATURE [PartDesign::Body] Body001  label="insertion_body"
  Group = -> [Sketch003,Pad001,Mirrored001]
  Origin = -> Origin001
  Tip = -> Mirrored001
COMPONENT P5 — geometry summary ("linear_bearing"; no construction recipe available for this part):
  bounding box: 78.0 x 44.0 x 25.4 mm
  tessellated surface: 4,410 triangles
  volume: 65645 mm^3 (75% of its bounding box)
  symmetry: 2-fold rotationally symmetric about the y axis; mirror-symmetric across its x mid-plane, z mid-plane
COMPONENT P6 — recipe-attached ("plywood", modeled in this document).
Construction recipe (the document's own serialized feature program — sketch geometry with constraints, then the solid features built on it; lengths are millimeters unless a unit is written):

FEATURE [Sketcher::SketchObject] Sketch005  label="plywood_sketch"
  FullyConstrained = true
  MapMode = 5
  Support = -> [XY_Plane003]
  sketch-geometry (5):
    g0: LineSegment StartX=-750 StartY=-750 StartZ=0 EndX=-750 EndY=750 EndZ=0
    g1: LineSegment StartX=-750 StartY=750 StartZ=0 EndX=750 EndY=750 EndZ=0
    g2: LineSegment StartX=750 StartY=750 StartZ=0 EndX=750 EndY=-750 EndZ=0
    g3: LineSegment StartX=750 StartY=-750 StartZ=0 EndX=-750 EndY=-750 EndZ=0
    g4: GeomPoint X=0 Y=-4.8e-15 Z=0
  constraints (12):
    c: Coincident(g0,g1)
    c: Coincident(g1,g2)
    c: Coincident(g2,g3)
    c: Coincident(g3,g0)
    c: Horizontal(g1)
    c: Horizontal(g3)
    c: Vertical(g0)
    c: Vertical(g2)
    c: Symmetric(g1,g0,g4)
    c: Coincident(g4,g-1)
    c: Distance(g3) = 1500  'width'
    c: DistanceY(g0,g0) = 1500  'length'
FEATURE [PartDesign::Pad] Pad002  label="plywood_pad"
  Direction = (0,0,1)
  Length = 24
  Length2 = 10
  Profile = -> Sketch005
  ReferenceAxis = -> Sketch005 [N_Axis]
  Type = 0
FEATURE [PartDesign::Body] Body003  label="plywood_body"
  Group = -> [Sketch005,Pad002]
  Origin = -> Origin003
  Tip = -> Pad002
COMPONENT P7 — recipe-attached ("plywood_material_end", modeled in this document).
Construction recipe (the document's own serialized feature program — sketch geometry with constraints, then the solid features built on it; lengths are millimeters unless a unit is written):

FEATURE [PartDesign::CoordinateSystem] LCS_0006
  AttacherType = Attacher::AttachEngine3D
  MapMode = 2
  Support = -> [X_Axis019]
FEATURE [Sketcher::SketchObject] Sketch018  label="plywood_material_end_sketch"
  FullyConstrained = true
  MapMode = 5
  Support = -> [XY_Plane020]
  sketch-geometry (5):
    g0: LineSegment StartX=0 StartY=0 StartZ=0 EndX=750 EndY=0 EndZ=0
    g1: LineSegment StartX=750 StartY=0 StartZ=0 EndX=750 EndY=1500 EndZ=0
    g2: LineSegment StartX=750 StartY=1500 StartZ=0 EndX=-750 EndY=1500 EndZ=0
    g3: LineSegment StartX=-750 StartY=1500 StartZ=0 EndX=-750 EndY=0 EndZ=0
    g4: LineSegment StartX=-750 StartY=0 StartZ=0 EndX=0 EndY=0 EndZ=0
  constraints (14):
    c: Coincident(g-1,g0)
    c: PointOnObject(g0,g-1)
    c: Coincident(g0,g1)
    c: Vertical(g1)
    c: Coincident(g1,g2)
    c: Horizontal(g2)
    c: Coincident(g2,g3)
    c: PointOnObject(g3,g-1)
    c: Vertical(g3)
    c: Coincident(g3,g4)
    c: Coincident(g4,g0)
    c: Equal(g4,g0)
    c: DistanceX(g3,g0) = 1500
    c: DistanceY(g1) = 1500
FEATURE [PartDesign::Pad] Pad016
  Direction = (0,0,1)
  Length = 10
  Length2 = 10
  Profile = -> Sketch018
  ReferenceAxis = -> Sketch018 [N_Axis]
  Type = 0
FEATURE [PartDesign::CoordinateSystem] plywood_end_top
  AttacherType = Attacher::AttachEngine3D
  AttachmentOffset = pos=(0,0,10) rot=(0,0,1;0rad)
  MapMode = 5
  Placement = pos=(0,0,10) rot=(0,0,1;0rad)
  Support = -> [XY_Plane020]
  expr: .AttachmentOffset.Base.z = Pad016.Length
FEATURE [PartDesign::Body] plywood_material_end
  Group = -> [LCS_0006,Sketch018,Pad016,plywood_end_top]
  Origin = -> Origin019
  Tip = -> Pad016
COMPONENT P8 — recipe-attached ("press_response_part", modeled in this document).
Construction recipe (the document's own serialized feature program — sketch geometry with constraints, then the solid features built on it; lengths are millimeters unless a unit is written):

FEATURE [PartDesign::CoordinateSystem] LCS_0005  label="end"
  AttacherType = Attacher::AttachEngine3D
  MapMode = 2
  Support = -> [X_Axis014]
FEATURE [Sketcher::SketchObject] Sketch_2
  FullyConstrained = true
  MapMode = 5
  Placement = pos=(0,0,0) rot=(1,0,0;1.5708rad)
  Support = -> [XZ_Plane014]
  sketch-geometry (5):
    g0: LineSegment StartX=-7.5 StartY=78.5 StartZ=0 EndX=-7.5 EndY=0 EndZ=0
    g1: LineSegment StartX=-7.5 StartY=0 StartZ=0 EndX=7.5 EndY=0 EndZ=0
    g2: LineSegment StartX=7.5 StartY=0 StartZ=0 EndX=7.5 EndY=78.5 EndZ=0
    g3: LineSegment StartX=7.5 StartY=78.5 StartZ=0 EndX=-7.5 EndY=78.5 EndZ=0
    g4: GeomPoint X=0 Y=39.25 Z=0
  constraints (13):
    c: Coincident(g0,g1)
    c: Coincident(g1,g2)
    c: Coincident(g2,g3)
    c: Coincident(g3,g0)
    c: Horizontal(g1)
    c: Horizontal(g3)
    c: Vertical(g0)
    c: Vertical(g2)
    c: Symmetric(g1,g0,g4)
    c: PointOnObject(g4,g-2)
    c: PointOnObject(g1,g-1)
    c: Distance(g1) = 15
    c: Distance(g2) = 78.5
FEATURE [PartDesign::Pad] Pad011
  Direction = (0,-1,-2e-16)
  Length = 900
  Length2 = 10
  Placement = pos=(0,0,0) rot=(1,0,0;1.5708rad)
  Profile = -> Sketch_2
  ReferenceAxis = -> Sketch_2 [N_Axis]
  Type = 0
FEATURE [PartDesign::CoordinateSystem] Local_CS001  label="begin"
  AttacherType = Attacher::AttachEngine3D
  AttachmentOffset = pos=(0,-900,0) rot=(0,0,1;0rad)
  MapMode = 5
  Placement = pos=(0,-900,0) rot=(0,0,1;0rad)
  Support = -> [XY_Plane014]
  expr: .AttachmentOffset.Base.y = -Pad011.Length
FEATURE [PartDesign::CoordinateSystem] Local_CS002
  AttacherType = Attacher::AttachEngine3D
  AttachmentOffset = pos=(0,-450,0) rot=(0,0,1;0rad)
  MapMode = 5
  Placement = pos=(0,-450,0) rot=(0,0,1;0rad)
  Support = -> [XY_Plane014]
  expr: .AttachmentOffset.Base.y = -Pad011.Length / 2
FEATURE [PartDesign::Body] press_response_part
  Group = -> [LCS_0005,Sketch_2,Pad011,Local_CS001,Local_CS002]
  Origin = -> Origin014
  Tip = -> Pad011
COMPONENT P9 — geometry summary ("roll"; no construction recipe available for this part):
  bounding box: 910.0 x 75.0 x 75.0 mm
  tessellated surface: 52 triangles
  volume: 2141375 mm^3 (42% of its bounding box)
  symmetry: 4-fold rotationally symmetric about the y axis; 2-fold rotationally symmetric about the z axis; mirror-symmetric across its x mid-plane, y mid-plane, z mid-plane
PROVENANCE & LICENSES
A FreeCAD (.FCStd) document from a public repository crawl; recipes are the document's own serialized feature recipes (and, for linked parts, companion documents' recipes).
License: as declared in the source repository (recorded in the dataset sidecar).
